# Revit family: QF_ELECTROLUXPROFESSIONAL_371115_E7WTNBN000
name_source: partatom
category: Specialty Equipment
revit_build: Autodesk Revit 2018 (Build: 20190510_1515(x64)
units: mm (PartAtom-declared; Revit-internal decimal feet)

## family parameters
Always vertical = Yes
Cut with Voids When Loaded = No
Part Type = Normal
Room Calculation Point = No
Round Connector Dimension = Use Diameter
Shared = No
Work Plane-Based = No

## types (1)
- QF_ELECTROLUXPROFESSIONAL_371115_E7WTNBN000
    Base Height = 24 mm
    Depth = 730 mm
    Description = 700XP 1/4 Module Ambient Worktop with Closed Front
    Direct Waste Size = 0"
    Height = 289 mm
    Manufacturer = ELECTROLUX
    Model = 371115
    URL = www.electrolux.com
    URL Cutsheet = www.electrolux.com
    Weight in Pounds = 0
    Width = 200 mm  [stored 0.656168 ft]

note: [stored X ft] marks values corroborated as IEEE doubles in the binary element streams (Revit-internal decimal feet)

## geometry (parser evidence)
native form markers: Blend x39, Sweep x2
no freeform markers — native parametric forms only
